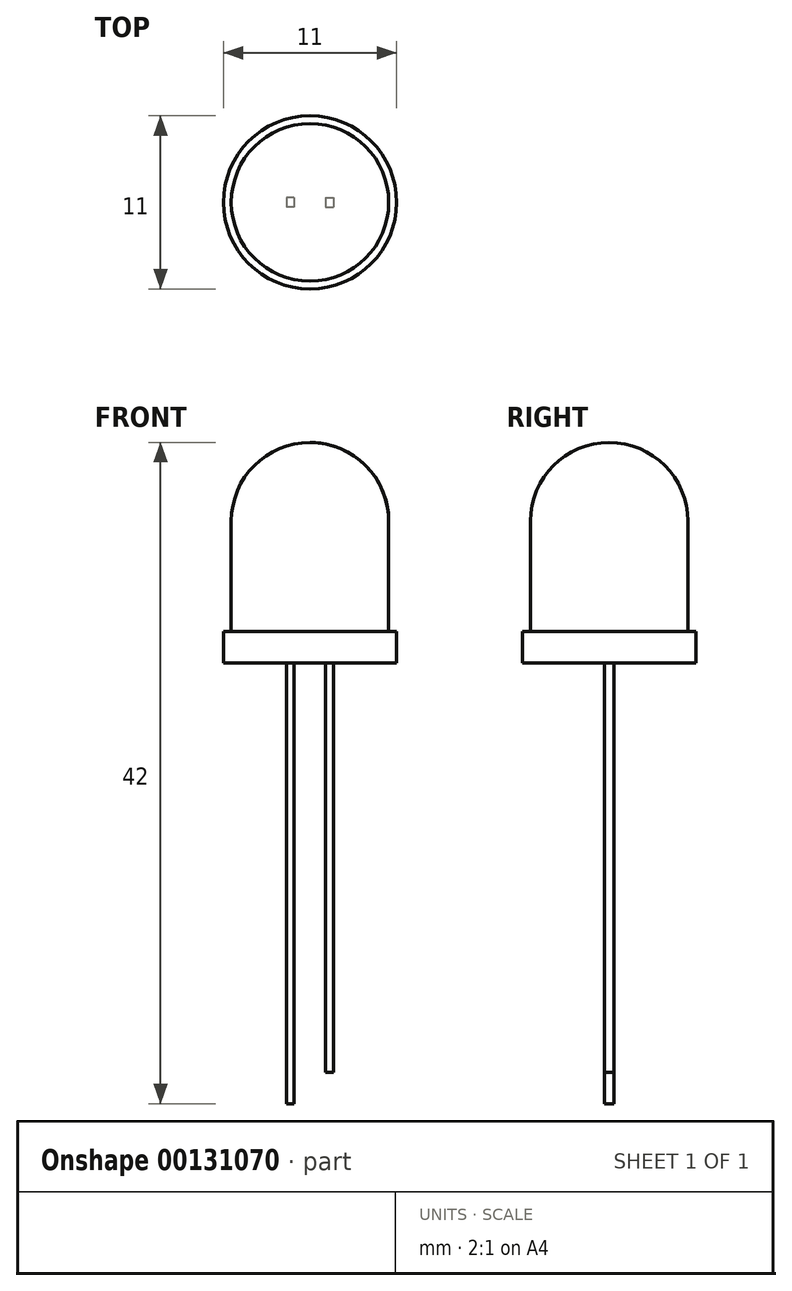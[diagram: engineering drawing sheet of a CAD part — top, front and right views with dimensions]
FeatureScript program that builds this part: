
annotation { "Feature Type Name" : "Feature", "Feature Type Description" : "" }
export const myFeature = defineFeature(function(context is Context, id is Id, definition is map)
    precondition{}
    {
        {
            var Q0;
            Q0=qCreatedBy(makeId("Top.planeOp"),FACE);
            var sketch = newSketch(context, id + "F0", { "sketchPlane" : qUnion([Q0])});
            skCircle(sketch, "E0", {"center": v(0, 0) * mm, "radius": 5 * mm});
            skSolve(sketch);
        }
        {
            var Q0;
            Q0=qSketchRegion(id+"F0",true);
            extrude(context, id + "F1", {"entities" : qUnion([Q0]), "depth" : 7 * mm, "offsetDistance" : 25.4 * mm});
        }
        {
            var Q0;
            Q0=qCreatedBy(makeId("Front.planeOp"),FACE);
            var sketch = newSketch(context, id + "F2", { "sketchPlane" : qUnion([Q0])});
            skLineSegment(sketch, "E1.0", {"start": v(-5, 7) * mm, "end": v(5, 7) * mm});
            skArc(sketch, "E2", {"start": v(5, 7) * mm, "mid": v(0, 12) * mm, "end": v(-5, 7) * mm});
            skLineSegment(sketch, "E3", {"start": v(0, 14) * mm, "end": v(0, 7) * mm});
            skSolve(sketch);
        }
        {
            var Q0;
            {var subQ0=sQuery(id+"F2.wireOp",EDGE,"E2");var subQ1=sQuery(id+"F2.wireOp",EDGE,"E1.0");var subQ2=makeQuery(id+"F2.imprint","INTERSECT",VERTEX,{"disambiguationData":[OD(1.0)],"derivedFrom":[subQ1,subQ0]});Q0=makeQuery(id+"F2.imprint","IMPRINT",FACE,{"disambiguationData":[TD([[makeQuery(id+"F2.imprint","IMPRINT",EDGE,{"disambiguationData":[TD([[subQ2,1.0]])],"derivedFrom":subQ1}),1.0]])]});}
            var Q1;
            Q1=sQuery(id+"F2.wireOp",EDGE,"E3");
            revolve(context, id + "F3", {"operationType" : NewBodyOperationType.ADD, "surfaceOperationType" : NewSurfaceOperationType.NEW, "entities" : qUnion([Q0]), "axis" : qUnion([Q1]), "revolveType" : RevolveType.FULL});
        }
        {
            var Q0;
            Q0=makeQuery(id+"F1.opExtrude","CAP_FACE",FACE,{"disambiguationData":[OSD([sQuery(id+"F0.wireOp",EDGE,"E0")])],"isStart":true});
            var sketch = newSketch(context, id + "F4", { "sketchPlane" : qUnion([Q0])});
            skCircle(sketch, "E4", {"center": v(0, 0) * mm, "radius": 5.5 * mm});
            skSolve(sketch);
        }
        {
            var Q0;
            Q0=makeQuery(id+"F4.imprint","IMPRINT",FACE,{"disambiguationData":[TD([[makeQuery(id+"F4.imprint","IMPRINT",EDGE,{"derivedFrom":sQuery(id+"F4.wireOp",EDGE,"E4")}),1.0]])]});
            var Q1;
            Q1=makeQuery(id+"F4.imprint","IMPRINT",FACE,{"disambiguationData":[TD([[makeQuery(id+"F4.imprint","IMPRINT",EDGE,{"derivedFrom":makeQuery(id+"F1.opExtrude","CAP_EDGE",EDGE,{"disambiguationData":[OSD([sQuery(id+"F0.wireOp",EDGE,"E0")])],"isStart":true})}),-1.0]])]});
            extrude(context, id + "F5", {"entities" : qUnion([Q0, Q1]), "operationType" : NewBodyOperationType.ADD, "depth" : 2 * mm, "offsetDistance" : 25.4 * mm});
        }
        {
            var Q0;
            Q0=makeQuery(id+"F5.opExtrude","CAP_FACE",FACE,{"disambiguationData":[OSD([sQuery(id+"F4.wireOp",EDGE,"E4")])],"isStart":false});
            var sketch = newSketch(context, id + "F6", { "sketchPlane" : qUnion([Q0])});
            skLineSegment(sketch, "E5", {"start": v(-1.25, 0) * mm, "end": v(1.25, 0) * mm});
            skLineSegment(sketch, "E6.bottom", {"start": v(1, -0.3) * mm, "end": v(1.5, -0.3) * mm});
            skLineSegment(sketch, "E6.top", {"start": v(1, 0.3) * mm, "end": v(1.5, 0.3) * mm});
            skLineSegment(sketch, "E6.left", {"start": v(1, -0.3) * mm, "end": v(1, 0.3) * mm});
            skLineSegment(sketch, "E6.right", {"start": v(1.5, -0.3) * mm, "end": v(1.5, 0.3) * mm});
            skPoint(sketch, "E6.middle", {"position": v(1.25, 0) * mm});
            skLineSegment(sketch, "E7", {"start": v(0, 0) * mm, "end": v(0, -2.7) * mm});
            skLineSegment(sketch, "E8.MirrorCS", {"start": v(-1, -0.3) * mm, "end": v(-1.5, -0.3) * mm});
            skPoint(sketch, "E9.MirrorP", {"position": v(-1.25, 0) * mm});
            skLineSegment(sketch, "E10.MirrorCS", {"start": v(-1.5, -0.3) * mm, "end": v(-1.5, 0.3) * mm});
            skLineSegment(sketch, "E11.MirrorCS", {"start": v(-1, 0.3) * mm, "end": v(-1.5, 0.3) * mm});
            skLineSegment(sketch, "E12.MirrorCS", {"start": v(-1, -0.3) * mm, "end": v(-1, 0.3) * mm});
            skSolve(sketch);
        }
        {
            var Q0;
            {var subQ1=sQuery(id+"F6.wireOp",EDGE,"E8.MirrorCS");Q0=makeQuery(id+"F6.imprint","IMPRINT",FACE,{"disambiguationData":[TD([[makeQuery(id+"F6.imprint","IMPRINT",EDGE,{"derivedFrom":subQ1}),-1.0]])]});}
            extrude(context, id + "F7", {"entities" : qUnion([Q0]), "operationType" : NewBodyOperationType.ADD, "depth" : 28 * mm, "offsetDistance" : 25.4 * mm});
        }
        {
            var Q0;
            {var subQ3=sQuery(id+"F6.wireOp",EDGE,"E6.bottom");Q0=makeQuery(id+"F6.imprint","IMPRINT",FACE,{"disambiguationData":[TD([[makeQuery(id+"F6.imprint","IMPRINT",EDGE,{"derivedFrom":subQ3}),1.0]])]});}
            extrude(context, id + "F8", {"entities" : qUnion([Q0]), "operationType" : NewBodyOperationType.ADD, "depth" : 26 * mm, "offsetDistance" : 25.4 * mm});
        }
    });
